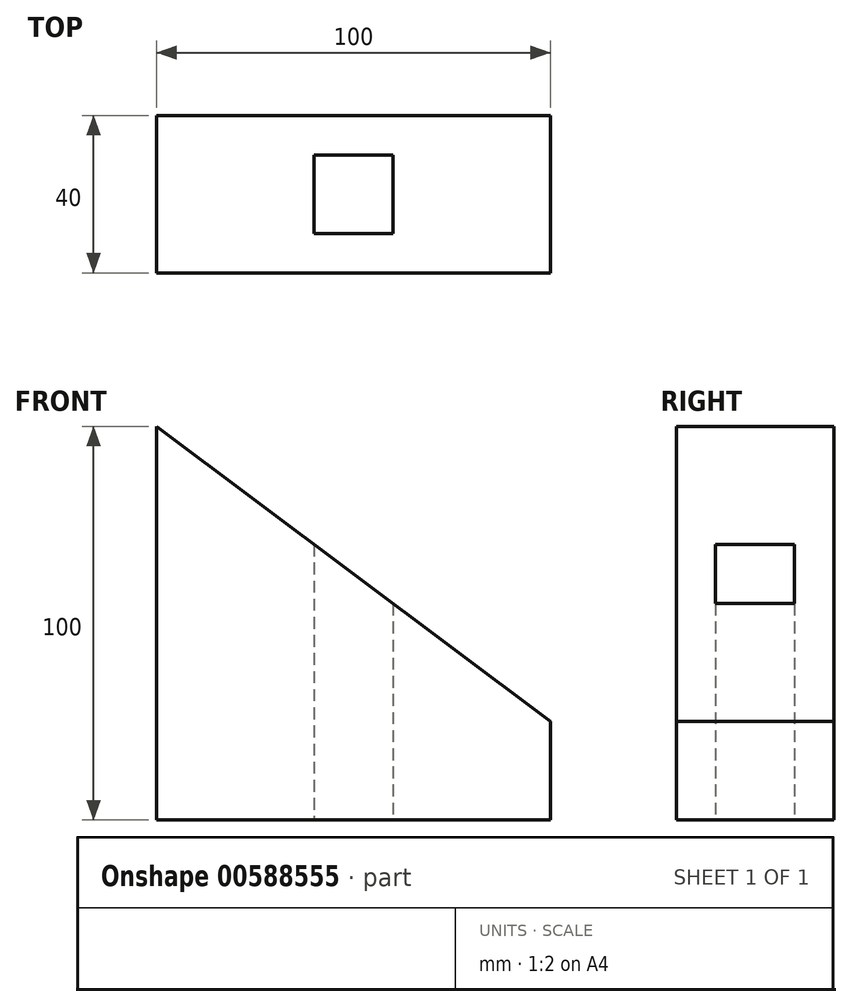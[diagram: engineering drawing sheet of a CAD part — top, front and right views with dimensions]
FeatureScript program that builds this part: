
annotation { "Feature Type Name" : "Feature", "Feature Type Description" : "" }
export const myFeature = defineFeature(function(context is Context, id is Id, definition is map)
    precondition{}
    {
        {
            var Q0;
            Q0=qCreatedBy(makeId("Front.planeOp"),FACE);
            var sketch = newSketch(context, id + "F0", { "sketchPlane" : qUnion([Q0])});
            skLineSegment(sketch, "E0", {"start": v(0, 0) * mm, "end": v(100, 0) * mm});
            skLineSegment(sketch, "E1", {"start": v(100, 0) * mm, "end": v(100, 25) * mm});
            skLineSegment(sketch, "E2", {"start": v(100, 25) * mm, "end": v(0, 100) * mm});
            skLineSegment(sketch, "E3", {"start": v(0, 100) * mm, "end": v(0, 100) * mm});
            skLineSegment(sketch, "E4", {"start": v(0, 100) * mm, "end": v(0, 0) * mm});
            skSolve(sketch);
        }
        {
            var Q0;
            Q0=makeQuery(id+"F0.imprint","IMPRINT",FACE,{"disambiguationData":[TD([[makeQuery(id+"F0.imprint","IMPRINT",EDGE,{"derivedFrom":sQuery(id+"F0.wireOp",EDGE,"E0")}),1.0]])]});
            extrude(context, id + "F1", {"entities" : qUnion([Q0]), "depth" : 40 * mm, "offsetDistance" : 25 * mm});
        }
        {
            var Q0;
            Q0=makeQuery(id+"F1.opExtrude","SWEPT_FACE",FACE,{"disambiguationData":[OSD([sQuery(id+"F0.wireOp",EDGE,"E0")])]});
            var sketch = newSketch(context, id + "F2", { "sketchPlane" : qUnion([Q0])});
            skLineSegment(sketch, "E5.bottom", {"start": v(40, 30) * mm, "end": v(60, 30) * mm});
            skLineSegment(sketch, "E5.top", {"start": v(40, 10) * mm, "end": v(60, 10) * mm});
            skLineSegment(sketch, "E5.left", {"start": v(40, 30) * mm, "end": v(40, 10) * mm});
            skLineSegment(sketch, "E5.right", {"start": v(60, 30) * mm, "end": v(60, 10) * mm});
            skSolve(sketch);
        }
        {
            var Q0;
            Q0=makeQuery(id+"F2.imprint","IMPRINT",FACE,{"disambiguationData":[TD([[makeQuery(id+"F2.imprint","IMPRINT",EDGE,{"derivedFrom":sQuery(id+"F2.wireOp",EDGE,"E5.bottom")}),-1.0]])]});
            extrude(context, id + "F3", {"entities" : qUnion([Q0]), "operationType" : NewBodyOperationType.REMOVE, "endBound" : BoundingType.THROUGH_ALL, "oppositeDirection" : true, "depth" : 25 * mm, "offsetDistance" : 25 * mm});
        }
    });
